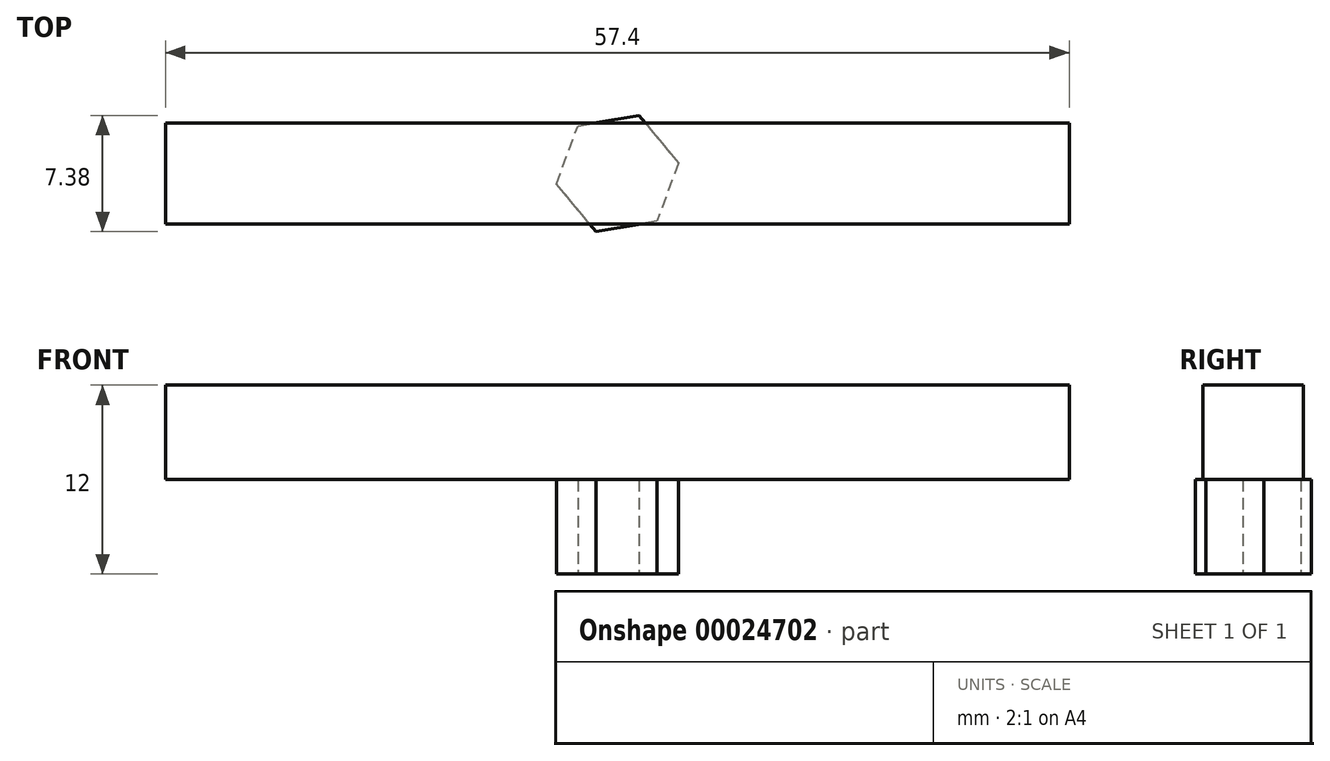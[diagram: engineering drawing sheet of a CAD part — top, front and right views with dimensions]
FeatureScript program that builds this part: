
annotation { "Feature Type Name" : "Feature", "Feature Type Description" : "" }
export const myFeature = defineFeature(function(context is Context, id is Id, definition is map)
    precondition{}
    {
        {
            var Q0;
            Q0=qCreatedBy(makeId("Top.planeOp"),FACE);
            var sketch = newSketch(context, id + "F0", { "sketchPlane" : qUnion([Q0])});
            skCircle(sketch, "E0.cCircle", {"center": v(0, 0) * mm, "radius": 25.68 * mm, "construction": true});
            skLineSegment(sketch, "E0.0", {"start": v(14.5, -21.2) * mm, "end": v(-11.1, -23.16) * mm});
            skLineSegment(sketch, "E0.1", {"start": v(-11.1, -23.16) * mm, "end": v(-25.6, -1.97) * mm});
            skLineSegment(sketch, "E0.2", {"start": v(-25.6, -1.97) * mm, "end": v(-14.5, 21.2) * mm});
            skLineSegment(sketch, "E0.3", {"start": v(-14.5, 21.2) * mm, "end": v(11.1, 23.16) * mm});
            skLineSegment(sketch, "E0.4", {"start": v(11.1, 23.16) * mm, "end": v(25.6, 1.97) * mm});
            skLineSegment(sketch, "E0.5", {"start": v(25.6, 1.97) * mm, "end": v(14.5, -21.2) * mm});
            skSolve(sketch);
        }
        {
            var Q0;
            Q0 = qSketchRegion(id + "F0", true);
            extrude(context, id + "F1", {"entities" : qUnion([Q0]), "depth" : 6 * mm});
        }
        {
            var Q0;
            Q0=makeQuery(id+"F1.opExtrude","CAP_FACE",FACE,{"disambiguationData":[OSD([sQuery(id+"F0.wireOp",EDGE,"E0.0"),sQuery(id+"F0.wireOp",EDGE,"E0.1"),sQuery(id+"F0.wireOp",EDGE,"E0.2"),sQuery(id+"F0.wireOp",EDGE,"E0.3"),sQuery(id+"F0.wireOp",EDGE,"E0.4"),sQuery(id+"F0.wireOp",EDGE,"E0.5")])],"isStart":false});
            var sketch = newSketch(context, id + "F2", { "sketchPlane" : qUnion([Q0])});
            skLineSegment(sketch, "E1.rect.bottom", {"start": v(28.26, 22.63) * mm, "end": v(-28.26, 22.63) * mm});
            skLineSegment(sketch, "E1.rect.top", {"start": v(28.26, -22.63) * mm, "end": v(-28.26, -22.63) * mm});
            skLineSegment(sketch, "E1.rect.left", {"start": v(28.26, 22.63) * mm, "end": v(28.26, -22.63) * mm});
            skLineSegment(sketch, "E1.rect.right", {"start": v(-28.26, 22.63) * mm, "end": v(-28.26, -22.63) * mm});
            skPoint(sketch, "E1.rect.middle", {"position": v(0, 0) * mm});
            skSolve(sketch);
        }
        {
            var Q0;
            {var subQ7=sQuery(id+"F2.wireOp",EDGE,"E1.rect.left");Q0=makeQuery(id+"F2.imprint","IMPRINT",FACE,{"disambiguationData":[TD([[makeQuery(id+"F2.imprint","IMPRINT",EDGE,{"derivedFrom":subQ7}),-1.0]])]});}
            var Q1;
            {var subQ7=sQuery(id+"F2.wireOp",EDGE,"E1.rect.right");Q1=makeQuery(id+"F2.imprint","IMPRINT",FACE,{"disambiguationData":[TD([[makeQuery(id+"F2.imprint","IMPRINT",EDGE,{"derivedFrom":subQ7}),1.0]])]});}
            extrude(context, id + "F3", {"entities" : qUnion([Q0, Q1]), "depth" : 6 * mm});
        }
        {
            var Q0;
            Q0=makeQuery(id+"F3.opExtrude","SWEPT_BODY",BODY,{"disambiguationData":[OSD([sQuery(id+"F0.wireOp",EDGE,"E0.0"),sQuery(id+"F0.wireOp",EDGE,"E0.4"),sQuery(id+"F0.wireOp",EDGE,"E0.5"),sQuery(id+"F2.wireOp",EDGE,"E1.rect.bottom"),sQuery(id+"F2.wireOp",EDGE,"E1.rect.top"),sQuery(id+"F2.wireOp",EDGE,"E1.rect.left")])]});
            deleteBodies(context, id + "F4", {"entities" : qUnion([Q0])});
        }
        {
            var Q0;
            Q0=makeQuery(id+"F3.opExtrude","SWEPT_BODY",BODY,{"disambiguationData":[OSD([sQuery(id+"F0.wireOp",EDGE,"E0.1"),sQuery(id+"F0.wireOp",EDGE,"E0.2"),sQuery(id+"F0.wireOp",EDGE,"E0.3"),sQuery(id+"F2.wireOp",EDGE,"E1.rect.bottom"),sQuery(id+"F2.wireOp",EDGE,"E1.rect.top"),sQuery(id+"F2.wireOp",EDGE,"E1.rect.right")])]});
            deleteBodies(context, id + "F5", {"entities" : qUnion([Q0])});
        }
        {
            var Q0;
            Q0=makeQuery(id+"F1.opExtrude","SWEPT_BODY",BODY,{"disambiguationData":[OSD([sQuery(id+"F0.wireOp",EDGE,"E0.0"),sQuery(id+"F0.wireOp",EDGE,"E0.1"),sQuery(id+"F0.wireOp",EDGE,"E0.2"),sQuery(id+"F0.wireOp",EDGE,"E0.3"),sQuery(id+"F0.wireOp",EDGE,"E0.4"),sQuery(id+"F0.wireOp",EDGE,"E0.5")])]});
            deleteBodies(context, id + "F6", {"entities" : qUnion([Q0])});
        }
        {
            var Q0;
            Q0=qCreatedBy(makeId("Top.planeOp"),FACE);
            var sketch = newSketch(context, id + "F7", { "sketchPlane" : qUnion([Q0])});
            skCircle(sketch, "E2.cCircle", {"center": v(0, 0) * mm, "radius": 3.4 * mm, "construction": true});
            skLineSegment(sketch, "E2.0", {"start": v(3.87, 0.67) * mm, "end": v(2.52, -3.02) * mm});
            skLineSegment(sketch, "E2.1", {"start": v(2.52, -3.02) * mm, "end": v(-1.36, -3.69) * mm});
            skLineSegment(sketch, "E2.2", {"start": v(-1.36, -3.69) * mm, "end": v(-3.87, -0.67) * mm});
            skLineSegment(sketch, "E2.3", {"start": v(-3.87, -0.67) * mm, "end": v(-2.52, 3.02) * mm});
            skLineSegment(sketch, "E2.4", {"start": v(-2.52, 3.02) * mm, "end": v(1.36, 3.69) * mm});
            skLineSegment(sketch, "E2.5", {"start": v(1.36, 3.69) * mm, "end": v(3.87, 0.67) * mm});
            skPoint(sketch, "E2.0.midPoint", {"position": v(3.2, -1.17) * mm});
            skSolve(sketch);
        }
        {
            var Q0;
            Q0 = qSketchRegion(id + "F7", true);
            extrude(context, id + "F8", {"entities" : qUnion([Q0]), "depth" : 6 * mm});
        }
        {
            var Q0;
            Q0=makeQuery(id+"F8.opExtrude","CAP_FACE",FACE,{"disambiguationData":[OSD([sQuery(id+"F7.wireOp",EDGE,"E2.0"),sQuery(id+"F7.wireOp",EDGE,"E2.1"),sQuery(id+"F7.wireOp",EDGE,"E2.2"),sQuery(id+"F7.wireOp",EDGE,"E2.3"),sQuery(id+"F7.wireOp",EDGE,"E2.4"),sQuery(id+"F7.wireOp",EDGE,"E2.5")])],"isStart":false});
            var sketch = newSketch(context, id + "F9", { "sketchPlane" : qUnion([Q0])});
            skLineSegment(sketch, "E3.rect.bottom", {"start": v(28.7, -3.2) * mm, "end": v(-28.7, -3.2) * mm});
            skLineSegment(sketch, "E3.rect.top", {"start": v(28.7, 3.2) * mm, "end": v(-28.7, 3.2) * mm});
            skLineSegment(sketch, "E3.rect.left", {"start": v(28.7, -3.2) * mm, "end": v(28.7, 3.2) * mm});
            skLineSegment(sketch, "E3.rect.right", {"start": v(-28.7, -3.2) * mm, "end": v(-28.7, 3.2) * mm});
            skPoint(sketch, "E3.rect.middle", {"position": v(0, 0) * mm});
            skSolve(sketch);
        }
        {
            var Q0;
            Q0 = qSketchRegion(id + "F9", true);
            var Q1;
            {var subQ7=sQuery(id+"F9.wireOp",EDGE,"E3.rect.left");Q1=makeQuery(id+"F9.imprint","IMPRINT",FACE,{"disambiguationData":[TD([[makeQuery(id+"F9.imprint","IMPRINT",EDGE,{"derivedFrom":subQ7}),1.0]])]});}
            extrude(context, id + "F10", {"entities" : qUnion([Q0, Q1]), "operationType" : NewBodyOperationType.ADD, "depth" : 6 * mm});
        }
    });
